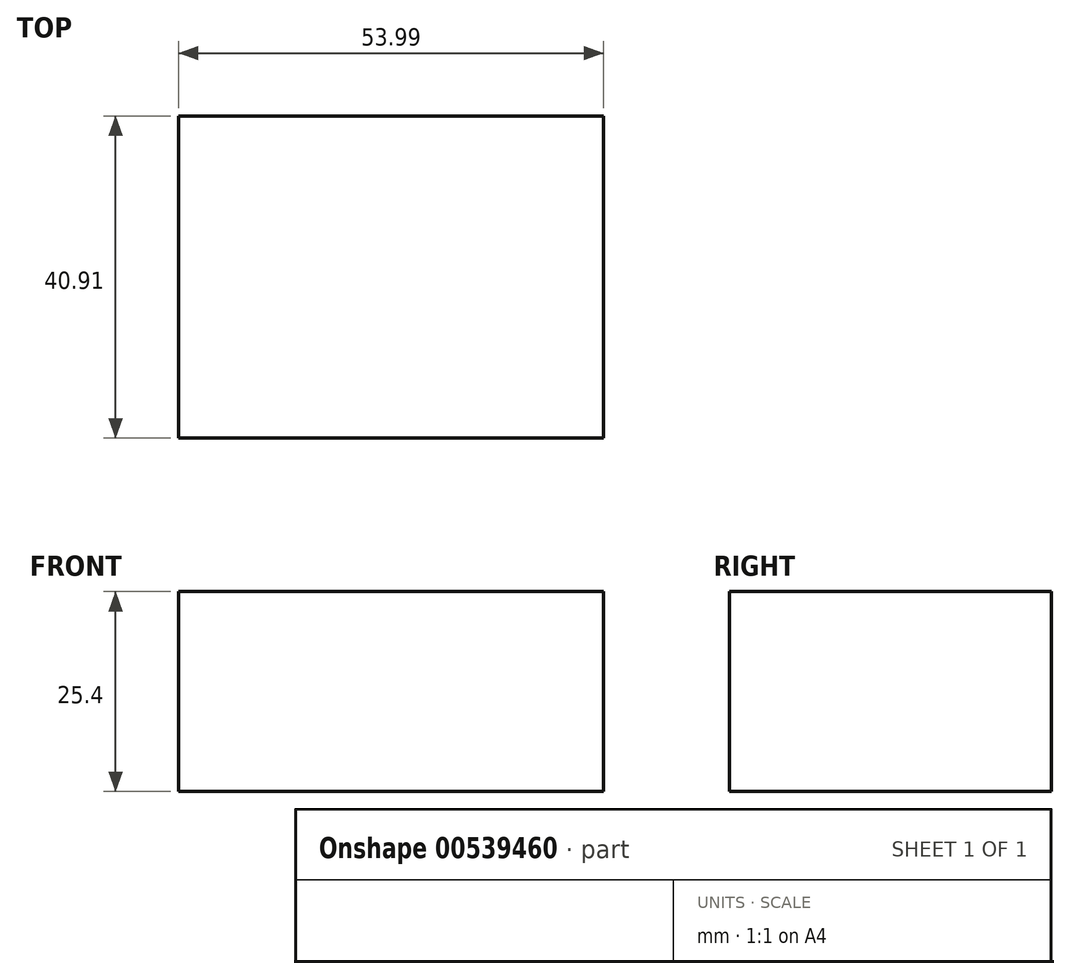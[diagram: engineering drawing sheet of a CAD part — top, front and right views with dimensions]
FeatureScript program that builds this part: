
annotation { "Feature Type Name" : "Feature", "Feature Type Description" : "" }
export const myFeature = defineFeature(function(context is Context, id is Id, definition is map)
    precondition{}
    {
        {
            var Q0;
            Q0=qCreatedBy(makeId("Top.planeOp"),FACE);
            var sketch = newSketch(context, id + "F0", { "sketchPlane" : qUnion([Q0])});
            skLineSegment(sketch, "E0", {"start": v(-98.02, 36.76) * mm, "end": v(26.58, 36.76) * mm});
            skLineSegment(sketch, "E1.bottom", {"start": v(-94.5, 21.4) * mm, "end": v(-40.5, 21.4) * mm});
            skLineSegment(sketch, "E1.top", {"start": v(-94.5, -19.52) * mm, "end": v(-40.5, -19.52) * mm});
            skLineSegment(sketch, "E1.left", {"start": v(-94.5, 21.4) * mm, "end": v(-94.5, -19.52) * mm});
            skLineSegment(sketch, "E1.right", {"start": v(-40.5, 21.4) * mm, "end": v(-40.5, -19.52) * mm});
            skSolve(sketch);
        }
        {
            var Q0;
            Q0=makeQuery(id+"F0.imprint","IMPRINT",FACE,{"disambiguationData":[TD([[makeQuery(id+"F0.imprint","IMPRINT",EDGE,{"derivedFrom":sQuery(id+"F0.wireOp",EDGE,"E1.bottom")}),-1.0]])]});
            extrude(context, id + "F1", {"entities" : qUnion([Q0]), "depth" : 25.4 * mm, "offsetDistance" : 25.4 * mm});
        }
    });
